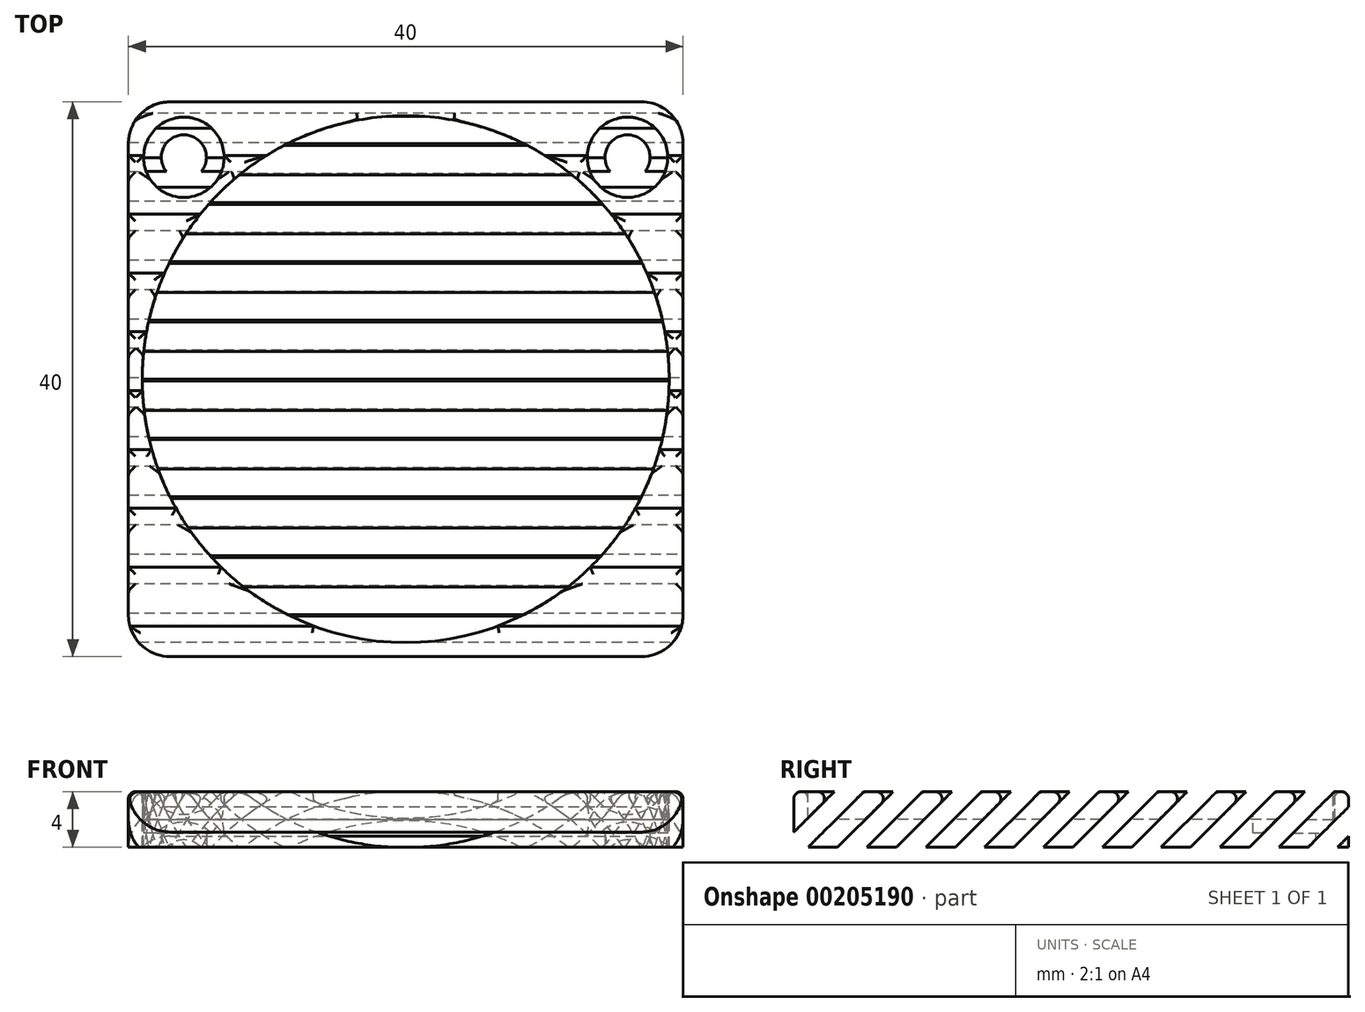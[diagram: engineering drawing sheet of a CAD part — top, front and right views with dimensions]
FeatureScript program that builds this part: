
annotation { "Feature Type Name" : "Feature", "Feature Type Description" : "" }
export const myFeature = defineFeature(function(context is Context, id is Id, definition is map)
    precondition{}
    {
        {
            var Q0;
            Q0=qCreatedBy(makeId("Top.planeOp"),FACE);
            var sketch = newSketch(context, id + "F0", { "sketchPlane" : qUnion([Q0])});
            skCircle(sketch, "E0", {"center": v(-16, 16) * mm, "radius": 1.63 * mm});
            skCircle(sketch, "E1", {"center": v(16, 16) * mm, "radius": 1.63 * mm});
            skCircle(sketch, "E2", {"center": v(16, -16) * mm, "radius": 1.63 * mm, "construction": true});
            skCircle(sketch, "E3", {"center": v(-16, -16) * mm, "radius": 1.63 * mm, "construction": true});
            skLineSegment(sketch, "E4", {"start": v(-16, 16) * mm, "end": v(16, -16) * mm, "construction": true});
            skPoint(sketch, "E5", {"position": v(0, 0) * mm});
            skSolve(sketch);
        }
        {
            var Q0;
            Q0=makeQuery(id+"F0.imprint","IMPRINT",FACE,{"disambiguationData":[TD([[makeQuery(id+"F0.imprint","IMPRINT",EDGE,{"derivedFrom":sQuery(id+"F0.wireOp",EDGE,"E0")}),1.0]])]});
            var sketch = newSketch(context, id + "F1", { "sketchPlane" : qUnion([Q0])});
            skLineSegment(sketch, "E6.bottom", {"start": v(17, -20) * mm, "end": v(-17, -20) * mm});
            skLineSegment(sketch, "E6.top", {"start": v(17, 20) * mm, "end": v(-17, 20) * mm});
            skLineSegment(sketch, "E6.left", {"start": v(20, -17) * mm, "end": v(20, 17) * mm});
            skLineSegment(sketch, "E6.right", {"start": v(-20, -17) * mm, "end": v(-20, 17) * mm});
            skPoint(sketch, "E6.middle", {"position": v(0, 0) * mm});
            skPoint(sketch, "E7.visualSharp", {"position": v(-20, 20) * mm});
            skArc(sketch, "E7.filletArc", {"start": v(-17, 20) * mm, "mid": v(-19.12, 19.12) * mm, "end": v(-20, 17) * mm});
            skPoint(sketch, "E8.visualSharp", {"position": v(20, 20) * mm});
            skArc(sketch, "E8.filletArc", {"start": v(20, 17) * mm, "mid": v(19.12, 19.12) * mm, "end": v(17, 20) * mm});
            skPoint(sketch, "E9.visualSharp", {"position": v(20, -20) * mm});
            skArc(sketch, "E9.filletArc", {"start": v(17, -20) * mm, "mid": v(19.12, -19.12) * mm, "end": v(20, -17) * mm});
            skPoint(sketch, "E10.visualSharp", {"position": v(-20, -20) * mm});
            skArc(sketch, "E10.filletArc", {"start": v(-20, -17) * mm, "mid": v(-19.12, -19.12) * mm, "end": v(-17, -20) * mm});
            skSolve(sketch);
        }
        {
            var Q0;
            Q0 = qSketchRegion(id + "F1", true);
            extrude(context, id + "F2", {"entities" : qUnion([Q0]), "depth" : 4 * mm});
        }
        {
            var Q0;
            Q0 = qSketchRegion(id + "F0", true);
            extrude(context, id + "F3", {"entities" : qUnion([Q0]), "operationType" : NewBodyOperationType.REMOVE, "endBound" : BoundingType.THROUGH_ALL, "depth" : 25 * mm});
        }
        {
            var Q0;
            Q0=makeQuery(id+"F2.opExtrude","CAP_FACE",FACE,{"disambiguationData":[OSD([sQuery(id+"F1.wireOp",EDGE,"E6.bottom"),sQuery(id+"F1.wireOp",EDGE,"E6.top"),sQuery(id+"F1.wireOp",EDGE,"E6.left"),sQuery(id+"F1.wireOp",EDGE,"E6.right"),sQuery(id+"F1.wireOp",EDGE,"E7.filletArc"),sQuery(id+"F1.wireOp",EDGE,"E8.filletArc"),sQuery(id+"F1.wireOp",EDGE,"E9.filletArc"),sQuery(id+"F1.wireOp",EDGE,"E10.filletArc")])],"isStart":false});
            var sketch = newSketch(context, id + "F4", { "sketchPlane" : qUnion([Q0])});
            skCircle(sketch, "E11", {"center": v(0, 0) * mm, "radius": 19 * mm});
            skSolve(sketch);
        }
        {
            var Q0;
            Q0 = qSketchRegion(id + "F4", true);
            extrude(context, id + "F5", {"entities" : qUnion([Q0]), "operationType" : NewBodyOperationType.REMOVE, "endBound" : BoundingType.THROUGH_ALL, "oppositeDirection" : true, "depth" : 2 * mm});
        }
        {
            var Q0;
            Q0 = qSketchRegion(id + "F4", true);
            extrude(context, id + "F6", {"entities" : qUnion([Q0]), "oppositeDirection" : true, "depth" : 2 * mm});
        }
        {
            var Q0;
            Q0=makeQuery(id+"F2.opExtrude","SWEPT_FACE",FACE,{"disambiguationData":[OSD([sQuery(id+"F1.wireOp",EDGE,"E6.left")])]});
            var sketch = newSketch(context, id + "F7", { "sketchPlane" : qUnion([Q0])});
            skLineSegment(sketch, "E12", {"start": v(2, 4) * mm, "end": v(-2, 0) * mm});
            skLineSegment(sketch, "E13.0", {"start": v(20, 2.9) * mm, "end": v(17.1, 0) * mm});
            skLineSegment(sketch, "E14.0", {"start": v(20, 0.79) * mm, "end": v(19.21, 0) * mm});
            skLineSegment(sketch, "E15.bottom", {"start": v(-17.1, 4) * mm, "end": v(-14.97, 4) * mm});
            skLineSegment(sketch, "E15.top", {"start": v(-20, 0) * mm, "end": v(-18.97, 0) * mm});
            skLineSegment(sketch, "E15.left", {"start": v(-20, 1.1) * mm, "end": v(-20, 0) * mm});
            skLineSegment(sketch, "E15.right", {"start": v(20, 2.9) * mm, "end": v(20, 0.79) * mm});
            skLineSegment(sketch, "E16.trimOffspring", {"start": v(18.97, 4) * mm, "end": v(14.97, 0) * mm});
            skLineSegment(sketch, "E17.trimOffspring", {"start": v(16.85, 4) * mm, "end": v(12.85, 0) * mm});
            skLineSegment(sketch, "E18.trimOffspring", {"start": v(14.73, 4) * mm, "end": v(10.73, 0) * mm});
            skLineSegment(sketch, "E19.trimOffspring", {"start": v(12.6, 4) * mm, "end": v(8.6, 0) * mm});
            skLineSegment(sketch, "E20.trimOffspring", {"start": v(10.49, 4) * mm, "end": v(6.49, 0) * mm});
            skLineSegment(sketch, "E21.trimOffspring", {"start": v(8.36, 4) * mm, "end": v(4.36, 0) * mm});
            skLineSegment(sketch, "E22.trimOffspring", {"start": v(6.24, 4) * mm, "end": v(2.24, 0) * mm});
            skLineSegment(sketch, "E23.trimOffspring", {"start": v(4.12, 4) * mm, "end": v(0.12, 0) * mm});
            skLineSegment(sketch, "E24.trimOffspring", {"start": v(-0.12, 4) * mm, "end": v(-4.12, 0) * mm});
            skLineSegment(sketch, "E25.trimOffspring", {"start": v(-2.24, 4) * mm, "end": v(-6.24, 0) * mm});
            skLineSegment(sketch, "E26.trimOffspring", {"start": v(-4.36, 4) * mm, "end": v(-8.36, 0) * mm});
            skLineSegment(sketch, "E27.trimOffspring", {"start": v(-6.49, 4) * mm, "end": v(-10.49, 0) * mm});
            skLineSegment(sketch, "E28.trimOffspring", {"start": v(-8.6, 4) * mm, "end": v(-12.6, 0) * mm});
            skLineSegment(sketch, "E29.trimOffspring", {"start": v(-10.73, 4) * mm, "end": v(-14.73, 0) * mm});
            skLineSegment(sketch, "E30.trimOffspring", {"start": v(-12.85, 4) * mm, "end": v(-16.85, 0) * mm});
            skLineSegment(sketch, "E31.trimOffspring", {"start": v(-14.97, 4) * mm, "end": v(-18.97, 0) * mm});
            skLineSegment(sketch, "E32.trimOffspring", {"start": v(-17.1, 4) * mm, "end": v(-20, 1.1) * mm});
            skLineSegment(sketch, "E33.trimOffspring", {"start": v(-16.85, 0) * mm, "end": v(-14.73, 0) * mm});
            skLineSegment(sketch, "E34.trimOffspring", {"start": v(-12.6, 0) * mm, "end": v(-10.49, 0) * mm});
            skLineSegment(sketch, "E35.trimOffspring", {"start": v(-8.36, 0) * mm, "end": v(-6.24, 0) * mm});
            skLineSegment(sketch, "E36.trimOffspring", {"start": v(-4.12, 0) * mm, "end": v(-2, 0) * mm});
            skLineSegment(sketch, "E37.trimOffspring", {"start": v(0.12, 0) * mm, "end": v(2.24, 0) * mm});
            skLineSegment(sketch, "E38.trimOffspring", {"start": v(4.36, 0) * mm, "end": v(6.49, 0) * mm});
            skLineSegment(sketch, "E39.trimOffspring", {"start": v(8.6, 0) * mm, "end": v(10.73, 0) * mm});
            skLineSegment(sketch, "E40.trimOffspring", {"start": v(12.85, 0) * mm, "end": v(14.97, 0) * mm});
            skLineSegment(sketch, "E41.trimOffspring", {"start": v(17.1, 0) * mm, "end": v(19.21, 0) * mm});
            skLineSegment(sketch, "E42.trimOffspring", {"start": v(16.85, 4) * mm, "end": v(18.97, 4) * mm});
            skLineSegment(sketch, "E43.trimOffspring", {"start": v(12.6, 4) * mm, "end": v(14.73, 4) * mm});
            skLineSegment(sketch, "E44.trimOffspring", {"start": v(8.36, 4) * mm, "end": v(10.49, 4) * mm});
            skLineSegment(sketch, "E45.trimOffspring", {"start": v(4.12, 4) * mm, "end": v(6.24, 4) * mm});
            skLineSegment(sketch, "E46.trimOffspring", {"start": v(-0.12, 4) * mm, "end": v(2, 4) * mm});
            skLineSegment(sketch, "E47.trimOffspring", {"start": v(-4.36, 4) * mm, "end": v(-2.24, 4) * mm});
            skLineSegment(sketch, "E48.trimOffspring", {"start": v(-8.6, 4) * mm, "end": v(-6.49, 4) * mm});
            skLineSegment(sketch, "E49.trimOffspring", {"start": v(-12.85, 4) * mm, "end": v(-10.73, 4) * mm});
            skSolve(sketch);
        }
        {
            var Q0;
            Q0 = qSketchRegion(id + "F7", true);
            extrude(context, id + "F8", {"entities" : qUnion([Q0]), "operationType" : NewBodyOperationType.REMOVE, "endBound" : BoundingType.THROUGH_ALL, "oppositeDirection" : true, "depth" : 25 * mm});
        }
        {
            var Q0;
            {var subQ0=sQuery(id+"F4.wireOp",EDGE,"E11");var subQ2=makeQuery(id+"F6.opExtrude","CAP_FACE",FACE,{"disambiguationData":[OSD([subQ0])],"isStart":true});Q0=makeQuery(id+"F11.opFillet","SPLIT",FACE,{"disambiguationData":[OD(0.0)],"derivedFrom":makeQuery(id+"FzWgOJvricvBhpY_2.opBoolean","MERGE",FACE,{"derivedFrom":[makeQuery(id+"F2.opExtrude","CAP_FACE",FACE,{"disambiguationData":[OSD([sQuery(id+"F1.wireOp",EDGE,"E6.bottom"),sQuery(id+"F1.wireOp",EDGE,"E6.top"),sQuery(id+"F1.wireOp",EDGE,"E6.left"),sQuery(id+"F1.wireOp",EDGE,"E6.right"),sQuery(id+"F1.wireOp",EDGE,"E7.filletArc"),sQuery(id+"F1.wireOp",EDGE,"E8.filletArc"),sQuery(id+"F1.wireOp",EDGE,"E9.filletArc"),sQuery(id+"F1.wireOp",EDGE,"E10.filletArc")])],"isStart":false}),makeQuery(id+"F8.boolean.opBoolean","SPLIT",FACE,{"disambiguationData":[TD([makeQuery(id+"F8.opExtrude","SWEPT_FACE",FACE,{"disambiguationData":[OSD([sQuery(id+"F7.wireOp",EDGE,"nO1I6wvn-3xJ7-ewn7-eeTk-p3WTNdZR4TWh")])]})])],"derivedFrom":subQ2}),makeQuery(id+"F8.boolean.opBoolean","SPLIT",FACE,{"disambiguationData":[TD([makeQuery(id+"F8.opExtrude","SWEPT_FACE",FACE,{"disambiguationData":[OSD([sQuery(id+"F7.wireOp",EDGE,"7552b35f-df75-4ebc-8272-74ec3b827858.0")])]})])],"derivedFrom":subQ2}),makeQuery(id+"F8.boolean.opBoolean","SPLIT",FACE,{"disambiguationData":[TD([makeQuery(id+"F8.opExtrude","SWEPT_FACE",FACE,{"disambiguationData":[OSD([sQuery(id+"F7.wireOp",EDGE,"583b9021-f11d-4a23-81bd-837db0680f54.0")])]})])],"derivedFrom":subQ2}),makeQuery(id+"F8.boolean.opBoolean","SPLIT",FACE,{"disambiguationData":[TD([makeQuery(id+"F8.opExtrude","SWEPT_FACE",FACE,{"disambiguationData":[OSD([sQuery(id+"F7.wireOp",EDGE,"7f978e1c-5897-4544-a430-e4fd1f4c6cb3.0")])]})])],"derivedFrom":subQ2}),makeQuery(id+"F8.boolean.opBoolean","SPLIT",FACE,{"disambiguationData":[TD([makeQuery(id+"F8.opExtrude","SWEPT_FACE",FACE,{"disambiguationData":[OSD([sQuery(id+"F7.wireOp",EDGE,"d6cb78da-631b-4943-869b-347c94565f9d.0")])]})])],"derivedFrom":subQ2}),makeQuery(id+"F8.boolean.opBoolean","SPLIT",FACE,{"disambiguationData":[TD([makeQuery(id+"F8.opExtrude","SWEPT_FACE",FACE,{"disambiguationData":[OSD([sQuery(id+"F7.wireOp",EDGE,"e67e771b-3e9a-4089-bc71-c3eb18524f08.0")])]})])],"derivedFrom":subQ2}),makeQuery(id+"F8.boolean.opBoolean","SPLIT",FACE,{"disambiguationData":[TD([makeQuery(id+"F8.opExtrude","SWEPT_FACE",FACE,{"disambiguationData":[OSD([sQuery(id+"F7.wireOp",EDGE,"1ecaff46-9f67-496a-add2-2dc0461393c0.0")])]})])],"derivedFrom":subQ2}),makeQuery(id+"F8.boolean.opBoolean","SPLIT",FACE,{"disambiguationData":[TD([makeQuery(id+"F8.opExtrude","SWEPT_FACE",FACE,{"disambiguationData":[OSD([sQuery(id+"F7.wireOp",EDGE,"ae444576-15e6-431e-932e-8c70d5e83652.0")])]})])],"derivedFrom":subQ2}),makeQuery(id+"F8.boolean.opBoolean","SPLIT",FACE,{"disambiguationData":[TD([makeQuery(id+"F8.opExtrude","SWEPT_FACE",FACE,{"disambiguationData":[OSD([sQuery(id+"F7.wireOp",EDGE,"992fc8b0-f619-4f81-923c-541e04878c92.0")])]})])],"derivedFrom":subQ2})]})});}
            var sketch = newSketch(context, id + "F9", { "sketchPlane" : qUnion([Q0])});
            skCircle(sketch, "E50", {"center": v(16, 16) * mm, "radius": 2.9 * mm});
            skCircle(sketch, "E51", {"center": v(-16, 16) * mm, "radius": 2.9 * mm});
            skSolve(sketch);
        }
        {
            var Q0;
            Q0 = qSketchRegion(id + "F9", true);
            extrude(context, id + "F10", {"entities" : qUnion([Q0]), "operationType" : NewBodyOperationType.REMOVE, "oppositeDirection" : true, "depth" : 3 * mm});
        }
        {
            var Q0;
            {var subQ0=sQuery(id+"F4.wireOp",EDGE,"E11");var subQ2=makeQuery(id+"F6.opExtrude","CAP_FACE",FACE,{"disambiguationData":[OSD([subQ0])],"isStart":true});Q0=makeQuery(id+"FzWgOJvricvBhpY_2.opBoolean","MERGE",FACE,{"derivedFrom":[makeQuery(id+"F2.opExtrude","CAP_FACE",FACE,{"disambiguationData":[OSD([sQuery(id+"F1.wireOp",EDGE,"E6.bottom"),sQuery(id+"F1.wireOp",EDGE,"E6.top"),sQuery(id+"F1.wireOp",EDGE,"E6.left"),sQuery(id+"F1.wireOp",EDGE,"E6.right"),sQuery(id+"F1.wireOp",EDGE,"E7.filletArc"),sQuery(id+"F1.wireOp",EDGE,"E8.filletArc"),sQuery(id+"F1.wireOp",EDGE,"E9.filletArc"),sQuery(id+"F1.wireOp",EDGE,"E10.filletArc")])],"isStart":false}),makeQuery(id+"F8.boolean.opBoolean","SPLIT",FACE,{"disambiguationData":[TD([makeQuery(id+"F8.opExtrude","SWEPT_FACE",FACE,{"disambiguationData":[OSD([sQuery(id+"F7.wireOp",EDGE,"nO1I6wvn-3xJ7-ewn7-eeTk-p3WTNdZR4TWh")])]})])],"derivedFrom":subQ2}),makeQuery(id+"F8.boolean.opBoolean","SPLIT",FACE,{"disambiguationData":[TD([makeQuery(id+"F8.opExtrude","SWEPT_FACE",FACE,{"disambiguationData":[OSD([sQuery(id+"F7.wireOp",EDGE,"7552b35f-df75-4ebc-8272-74ec3b827858.0")])]})])],"derivedFrom":subQ2}),makeQuery(id+"F8.boolean.opBoolean","SPLIT",FACE,{"disambiguationData":[TD([makeQuery(id+"F8.opExtrude","SWEPT_FACE",FACE,{"disambiguationData":[OSD([sQuery(id+"F7.wireOp",EDGE,"583b9021-f11d-4a23-81bd-837db0680f54.0")])]})])],"derivedFrom":subQ2}),makeQuery(id+"F8.boolean.opBoolean","SPLIT",FACE,{"disambiguationData":[TD([makeQuery(id+"F8.opExtrude","SWEPT_FACE",FACE,{"disambiguationData":[OSD([sQuery(id+"F7.wireOp",EDGE,"7f978e1c-5897-4544-a430-e4fd1f4c6cb3.0")])]})])],"derivedFrom":subQ2}),makeQuery(id+"F8.boolean.opBoolean","SPLIT",FACE,{"disambiguationData":[TD([makeQuery(id+"F8.opExtrude","SWEPT_FACE",FACE,{"disambiguationData":[OSD([sQuery(id+"F7.wireOp",EDGE,"d6cb78da-631b-4943-869b-347c94565f9d.0")])]})])],"derivedFrom":subQ2}),makeQuery(id+"F8.boolean.opBoolean","SPLIT",FACE,{"disambiguationData":[TD([makeQuery(id+"F8.opExtrude","SWEPT_FACE",FACE,{"disambiguationData":[OSD([sQuery(id+"F7.wireOp",EDGE,"e67e771b-3e9a-4089-bc71-c3eb18524f08.0")])]})])],"derivedFrom":subQ2}),makeQuery(id+"F8.boolean.opBoolean","SPLIT",FACE,{"disambiguationData":[TD([makeQuery(id+"F8.opExtrude","SWEPT_FACE",FACE,{"disambiguationData":[OSD([sQuery(id+"F7.wireOp",EDGE,"1ecaff46-9f67-496a-add2-2dc0461393c0.0")])]})])],"derivedFrom":subQ2}),makeQuery(id+"F8.boolean.opBoolean","SPLIT",FACE,{"disambiguationData":[TD([makeQuery(id+"F8.opExtrude","SWEPT_FACE",FACE,{"disambiguationData":[OSD([sQuery(id+"F7.wireOp",EDGE,"ae444576-15e6-431e-932e-8c70d5e83652.0")])]})])],"derivedFrom":subQ2}),makeQuery(id+"F8.boolean.opBoolean","SPLIT",FACE,{"disambiguationData":[TD([makeQuery(id+"F8.opExtrude","SWEPT_FACE",FACE,{"disambiguationData":[OSD([sQuery(id+"F7.wireOp",EDGE,"992fc8b0-f619-4f81-923c-541e04878c92.0")])]})])],"derivedFrom":subQ2})]});}
            fillet(context, id + "F11", {"entities" : qUnion([Q0]), "radius" : .5 * mm, "tangentPropagation" : true, "allowEdgeOverflow" : false});
        }
    });
